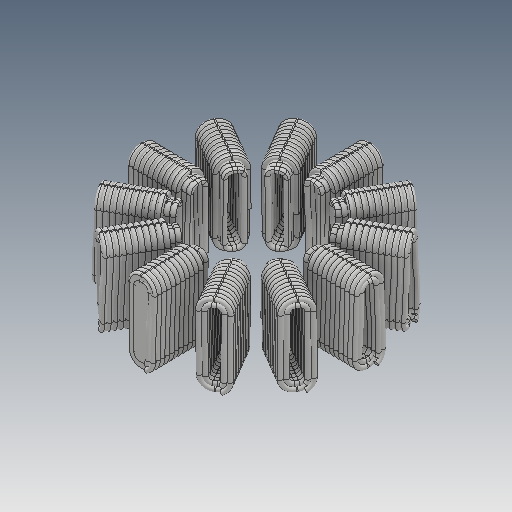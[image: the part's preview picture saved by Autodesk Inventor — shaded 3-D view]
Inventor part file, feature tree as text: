
AUTODESK INVENTOR PART (.ipt)
format: ipt  version: 2018 (Build 220112000, 112)  size: 39,801,344 bytes
history: native  units: mm
features: other x24, sweep x2
ambient origin geometry x8: Origin, YZ Plane, XZ Plane, XY Plane, X Axis, Y Axis, Z Axis, Center Point
bodies: Volumenkörper1 (feature_tree), Volumenkörper2 (feature_tree), Volumenkörper3 (feature_tree), Volumenkörper4 (feature_tree), Volumenkörper5 (feature_tree), Volumenkörper6 (feature_tree), Volumenkörper7 (feature_tree), Volumenkörper8 (feature_tree), Volumenkörper9 (feature_tree), Volumenkörper10 (feature_tree), Volumenkörper11 (feature_tree), Volumenkörper12 (feature_tree), Volumenkörper13 (feature_tree), Volumenkörper14 (feature_tree), Volumenkörper15 (feature_tree), Volumenkörper16 (feature_tree), Volumenkörper17 (feature_tree), Volumenkörper18 (feature_tree), Volumenkörper19 (feature_tree), Volumenkörper20 (feature_tree), Volumenkörper21 (feature_tree), Volumenkörper22 (feature_tree), Volumenkörper23 (feature_tree), Volumenkörper24 (feature_tree), Volumenkörper25 (feature_tree), Volumenkörper26 (feature_tree)
feature tree (26):
  other  "Boss-Extrude2"
  other  "Boss-Extrude3"
  sweep  "Sweep3"
  sweep  "Sweep4"
  other  "CirPattern1[1]"
  other  "CirPattern1[2]"
  other  "CirPattern1[3]"
  other  "CirPattern1[4]"
  other  "CirPattern1[5]"
  other  "CirPattern1[6]"
  other  "CirPattern1[7]"
  other  "CirPattern1[8]"
  other  "CirPattern1[9]"
  other  "CirPattern1[10]"
  other  "CirPattern1[11]"
  other  "CirPattern1[12]"
  other  "CirPattern1[13]"
  other  "CirPattern1[14]"
  other  "CirPattern1[15]"
  other  "CirPattern1[16]"
  other  "CirPattern1[17]"
  other  "CirPattern1[18]"
  other  "CirPattern1[19]"
  other  "CirPattern1[20]"
  other  "CirPattern1[21]"
  other  "CirPattern1[22]"
